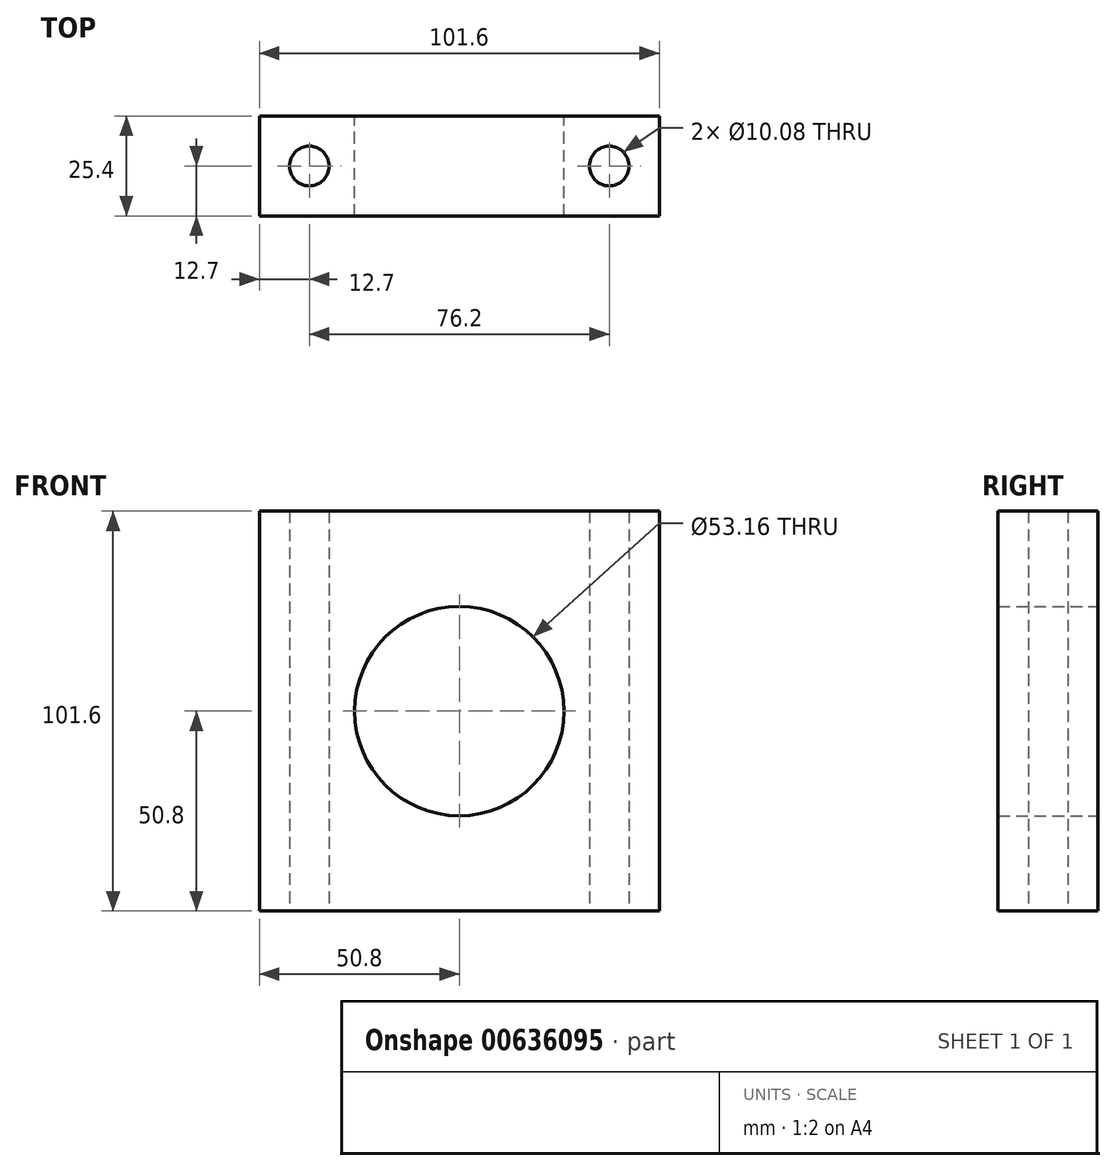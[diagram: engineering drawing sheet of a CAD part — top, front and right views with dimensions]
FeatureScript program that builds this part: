
annotation { "Feature Type Name" : "Feature", "Feature Type Description" : "" }
export const myFeature = defineFeature(function(context is Context, id is Id, definition is map)
    precondition{}
    {
        {
            var Q0;
            Q0=qCreatedBy(makeId("Front.planeOp"),FACE);
            var sketch = newSketch(context, id + "F0", { "sketchPlane" : qUnion([Q0])});
            skCircle(sketch, "E0", {"center": v(0, 0) * mm, "radius": 26.58 * mm});
            skLineSegment(sketch, "E1.bottom", {"start": v(50.8, 50.8) * mm, "end": v(-50.8, 50.8) * mm});
            skLineSegment(sketch, "E1.top", {"start": v(50.8, -50.8) * mm, "end": v(-50.8, -50.8) * mm});
            skLineSegment(sketch, "E1.left", {"start": v(50.8, 50.8) * mm, "end": v(50.8, -50.8) * mm});
            skLineSegment(sketch, "E1.right", {"start": v(-50.8, 50.8) * mm, "end": v(-50.8, -50.8) * mm});
            skSolve(sketch);
        }
        {
            var Q0;
            Q0=makeQuery(id+"F0.imprint","IMPRINT",FACE,{"disambiguationData":[TD([[makeQuery(id+"F0.imprint","IMPRINT",EDGE,{"derivedFrom":sQuery(id+"F0.wireOp",EDGE,"E0")}),-1.0]])]});
            extrude(context, id + "F1", {"entities" : qUnion([Q0]), "depth" : 25.4 * mm, "offsetDistance" : 25.4 * mm});
        }
        {
            var Q0;
            Q0=makeQuery(id+"F1.opExtrude","SWEPT_FACE",FACE,{"disambiguationData":[OSD([sQuery(id+"F0.wireOp",EDGE,"E1.top")])]});
            var sketch = newSketch(context, id + "F2", { "sketchPlane" : qUnion([Q0])});
            skCircle(sketch, "E2", {"center": v(38.1, 12.7) * mm, "radius": 5.04 * mm});
            skCircle(sketch, "E3", {"center": v(-38.1, 12.7) * mm, "radius": 5.04 * mm});
            skPoint(sketch, "E3.centerSnap0", {"position": v(-50.8, 12.7) * mm});
            skSolve(sketch);
        }
        {
            var Q0;
            Q0=makeQuery(id+"F2.imprint","IMPRINT",FACE,{"disambiguationData":[TD([[makeQuery(id+"F2.imprint","IMPRINT",EDGE,{"derivedFrom":sQuery(id+"F2.wireOp",EDGE,"E3")}),1.0]])]});
            var Q1;
            Q1=makeQuery(id+"F2.imprint","IMPRINT",FACE,{"disambiguationData":[TD([[makeQuery(id+"F2.imprint","IMPRINT",EDGE,{"derivedFrom":sQuery(id+"F2.wireOp",EDGE,"E2")}),1.0]])]});
            extrude(context, id + "F3", {"entities" : qUnion([Q0, Q1]), "operationType" : NewBodyOperationType.REMOVE, "endBound" : BoundingType.THROUGH_ALL, "oppositeDirection" : true, "depth" : 25.4 * mm, "offsetDistance" : 25.4 * mm});
        }
    });
